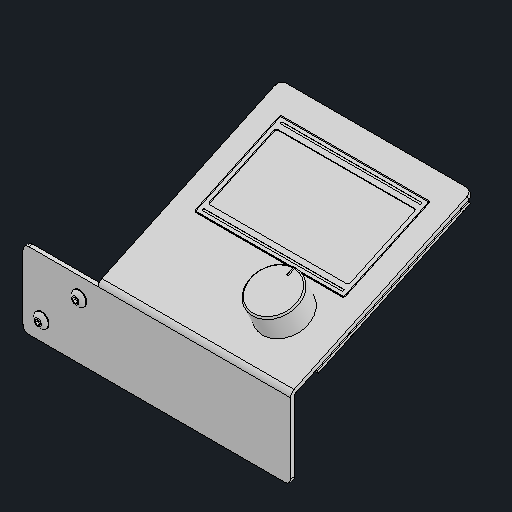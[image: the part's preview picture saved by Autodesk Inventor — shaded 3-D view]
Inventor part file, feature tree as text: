
AUTODESK INVENTOR PART (.ipt)
format: ipt  version: 2024.2 (Build 282272000, 272)  size: 1,350,656 bytes
history: native  units: mm
features: other x35, mirror x3, fillet x1, chamfer x1
ambient origin geometry x8: Origin, YZ Plane, XZ Plane, XY Plane, X Axis, Y Axis, Z Axis, Center Point
bodies: Body1 (feature_tree), Body2 (feature_tree), Body3 (feature_tree), Body4 (feature_tree), Body5 (feature_tree), Body6 (feature_tree), Body7 (feature_tree), Body8 (feature_tree), Body9 (feature_tree), Body10 (feature_tree), Body11 (feature_tree), Body12 (feature_tree), Body13 (feature_tree), Body14 (feature_tree), Body15 (feature_tree), Body16 (feature_tree), Body17 (feature_tree), Body18 (feature_tree), Body19 (feature_tree), Body20 (feature_tree)
feature tree (40):
  other  "솔리드1"
  other  "솔리드2"
  other  "솔리드3"
  other  "솔리드4"
  other  "솔리드5"
  other  "솔리드6"
  other  "솔리드7"
  other  "솔리드8"
  other  "솔리드9"
  other  "솔리드10"
  other  "솔리드11"
  other  "솔리드12"
  other  "솔리드13"
  other  "솔리드14"
  other  "솔리드15"
  other  "솔리드16"
  other  "솔리드17"
  other  "솔리드18"
  other  "솔리드19"
  other  "솔리드20"
  other  "Boss-Extrude2-pcb"
  other  "Boss-Extrude3-pcb"
  other  "M3x0.5 Tapped Hole1-pcb-screw-bosses"
  other  "Body-Move_Copy1-pcb-screw-bosses"
  mirror  "Mirror1-pcb-screw-bosses[1]"
  mirror  "Mirror1-pcb-screw-bosses[2]"
  other  "Body-Move_Copy2-pcb[1]"
  other  "Body-Move_Copy2-pcb[2]"
  other  "Cut-Extrude5-pcb"
  fillet  "Fillet14-display-frame"  [1 undecoded]
  other  "Boss-Extrude13-display-glass"
  chamfer  "Chamfer2-knob"  [1 undecoded]
  other  "_bhcs-M4_-_ThdSchPat_"
  other  "_bhcs-M4_-_ThdSchPat_:1"
  other  "_t-slot-nut_-_M4x0.7 Tapped Hole1_"
  other  "_t-slot-nut_-_M4x0.7 Tapped Hole1_:1"
  other  "_bhcs-M3_-_ThdSchPat_"
  mirror  "Mirror1"
  other  "Body-Move_Copy11[1]"
  other  "Body-Move_Copy11[2]"
note: 2 required parameter values undecoded (feature->parameter linkage not recoverable at this tier; creation-order binding heuristic only, values carry confidence <= 0.55)
